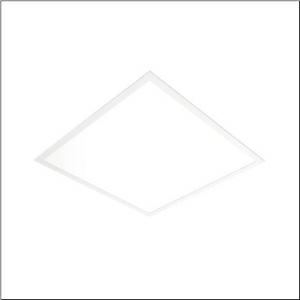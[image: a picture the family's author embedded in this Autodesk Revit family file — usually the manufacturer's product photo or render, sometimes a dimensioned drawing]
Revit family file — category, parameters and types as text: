
# Revit family: apollon_r__41_51mh11wd2n43_c469
name_source: partatom
category: Lighting Fixtures
units: mm (PartAtom-declared; Revit-internal decimal feet)

## family parameters
Cut with Voids When Loaded = No
Host = Face
Light Source = No
Part Type = Normal
Room Calculation Point = No
Round Connector Dimension = Use Diameter
Shared = No

## types (1)
- --- (1 x LED, 3450 lm, 28.5 W, 6500K)
    Apparent Load = 29 VA
    CIE Flux Codes = 61 87 97 100 100
    Color Rendering = 80
    Color Temperature = 6500K
    Default Elevation = 1800 mm
    Description = Apollon® 41, office luminaire, primary optical cover: prismatic diffuser, of PS, light emission: direct distribution, primary light characteristic: symmetric, installation type: lay-in mounting, LED, rated luminous flux: 3.500lm, luminous efficacy: 123lm/W, light colour: 840/865, colour temperature: 4000/6500K, control gear: DALI 2, with terminal, 5-pole, mains connection: 220..240V, AC, 50/60Hz, suitable for self-contained emergency lighting element 58DB00B013A with integrated self-test function according to EN 60598-2-22, housing, of aluminium section, traffic white (RAL 9016), module: M625, length: 620mm, width: 620mm, height: 60mm, recess depth: 180mm, housing upper side, of sheet steel, protection rating (complete): IP20, protection rating (lamp compartment, on room side): IP40, insulation class (complete): insulation class II (safety insulation), certification: CE, ENEC, impact resistance: IK03, permissible operating ambient temperature: -25..+40°C, packaging unit: 1 piece
    Height = 0 mm  [stored 0 ft]
    Lamp = 1 x LED
    Lamp Light Flux = 3450 lm
    Lamp Power = 28.5 W
    Lamp count = 1
    Length = 620 mm
    Luminous efficacy = 121 lm/W
    Manufacturer = Siteco
    ModVariant = No
    Model = 51MH11WD2N43
    Mounting Place = Ceiling
    Mounting Type = Recessed
    Number of Poles = 1
    OnlyDefault = Yes
    Power Factor = 1
    Product Name = Apollon® 41
    Product group = office luminaire | ceiling recessed
    ProductGroupID = 400
    Protection Class = Protection class II
    Protection Degree = IP 20
    RLX_Detail_Level = 1
    RLX_Emergency_Light_Flux = 0 lm
    RLX_Emergency_Type = 0
    RLX_Emergency_Type_DB = No
    RlxData = <blob elided: 12637 chars, md5=5672a8c0>
    Socket = socket
    Standby Power = 0 W
    System Light Flux = 3450 lm
    System Power = 29 W
    Type Comments = individual setting
    Type Image = l_1291024.jpg
    URL = http://relux.com
    VarID = @adj_098119
    Voltage = 0 V
    Weight = 0.00 kg
    Width = 620 mm

note: [stored X ft] marks values corroborated as IEEE doubles in the binary element streams (Revit-internal decimal feet)

## geometry (parser evidence)
native form markers: Sweep x8
no freeform markers — native parametric forms only
